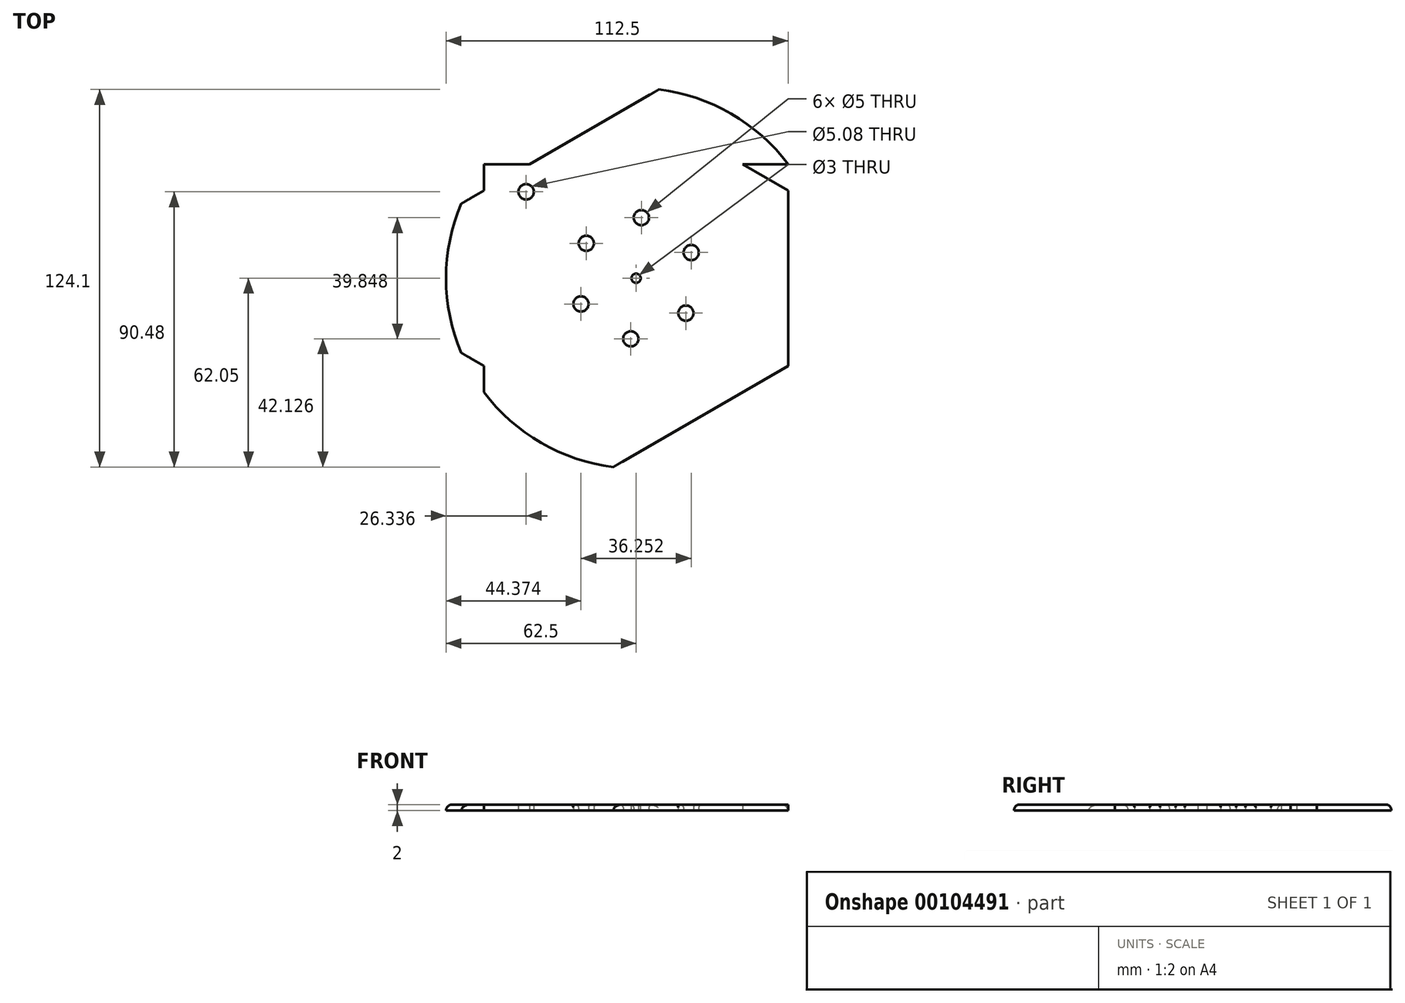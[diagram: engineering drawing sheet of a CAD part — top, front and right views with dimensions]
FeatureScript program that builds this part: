
annotation { "Feature Type Name" : "Feature", "Feature Type Description" : "" }
export const myFeature = defineFeature(function(context is Context, id is Id, definition is map)
    precondition{}
    {
        {
            var Q0;
            Q0=qCreatedBy(makeId("Top.planeOp"),FACE);
            var sketch = newSketch(context, id + "F0", { "sketchPlane" : qUnion([Q0])});
            skLineSegment(sketch, "E0.bottom", {"start": v(50, -37.5) * mm, "end": v(-50, -37.5) * mm});
            skLineSegment(sketch, "E0.top", {"start": v(50, 37.5) * mm, "end": v(-50, 37.5) * mm});
            skLineSegment(sketch, "E0.left", {"start": v(50, -37.5) * mm, "end": v(50, 37.5) * mm});
            skLineSegment(sketch, "E0.right", {"start": v(-50, -37.5) * mm, "end": v(-50, 37.5) * mm});
            skPoint(sketch, "E0.middle", {"position": v(0, 0) * mm});
            skCircle(sketch, "E1", {"center": v(-16.38, 11.47) * mm, "radius": 2.5 * mm});
            skLineSegment(sketch, "E2", {"start": v(0, 0) * mm, "end": v(-16.38, 11.47) * mm, "construction": true});
            skLineSegment(sketch, "E3", {"start": v(0, 0) * mm, "end": v(-16.38, 0) * mm, "construction": true});
            skCircle(sketch, "E4.1.0", {"center": v(-18.13, -8.45) * mm, "radius": 2.5 * mm});
            skLineSegment(sketch, "E4.1.1", {"start": v(0, 0) * mm, "end": v(-8.2, -14.19) * mm, "construction": true});
            skLineSegment(sketch, "E4.1.3", {"start": v(0, 0) * mm, "end": v(-18.13, -8.45) * mm, "construction": true});
            skLineSegment(sketch, "E4.1.4", {"start": v(7.48, -62.05) * mm, "end": v(-57.48, -24.55) * mm});
            skCircle(sketch, "E4.2.0", {"center": v(-1.74, -19.92) * mm, "radius": 2.5 * mm});
            skLineSegment(sketch, "E4.2.1", {"start": v(0, 0) * mm, "end": v(8.2, -14.19) * mm, "construction": true});
            skLineSegment(sketch, "E4.2.3", {"start": v(0, 0) * mm, "end": v(-1.74, -19.92) * mm, "construction": true});
            skLineSegment(sketch, "E4.2.4", {"start": v(57.48, -24.55) * mm, "end": v(-7.48, -62.05) * mm});
            skCircle(sketch, "E4.3.0", {"center": v(16.38, -11.47) * mm, "radius": 2.5 * mm});
            skLineSegment(sketch, "E4.3.1", {"start": v(0, 0) * mm, "end": v(16.38, 0) * mm, "construction": true});
            skLineSegment(sketch, "E4.3.3", {"start": v(0, 0) * mm, "end": v(16.38, -11.47) * mm, "construction": true});
            skLineSegment(sketch, "E4.3.4", {"start": v(50, 37.5) * mm, "end": v(50, -37.5) * mm});
            skCircle(sketch, "E4.4.0", {"center": v(18.13, 8.45) * mm, "radius": 2.5 * mm});
            skLineSegment(sketch, "E4.4.1", {"start": v(0, 0) * mm, "end": v(8.2, 14.19) * mm, "construction": true});
            skLineSegment(sketch, "E4.4.3", {"start": v(0, 0) * mm, "end": v(18.13, 8.45) * mm, "construction": true});
            skLineSegment(sketch, "E4.4.4", {"start": v(-7.48, 62.05) * mm, "end": v(57.48, 24.55) * mm});
            skCircle(sketch, "E4.5.0", {"center": v(1.74, 19.92) * mm, "radius": 2.5 * mm});
            skLineSegment(sketch, "E4.5.1", {"start": v(0, 0) * mm, "end": v(-8.2, 14.19) * mm, "construction": true});
            skLineSegment(sketch, "E4.5.3", {"start": v(0, 0) * mm, "end": v(1.74, 19.92) * mm, "construction": true});
            skLineSegment(sketch, "E4.5.4", {"start": v(-57.48, 24.55) * mm, "end": v(7.48, 62.05) * mm});
            skCircle(sketch, "E5", {"center": v(-36.16, 28.43) * mm, "radius": 2.54 * mm});
            skCircle(sketch, "E6", {"center": v(0, 0) * mm, "radius": 62.5 * mm});
            skSolve(sketch);
        }
        {
            var Q0;
            Q0=makeQuery(id+"F0.imprint","IMPRINT",FACE,{"disambiguationData":[TD([[makeQuery(id+"F0.imprint","IMPRINT",EDGE,{"derivedFrom":sQuery(id+"F0.wireOp",EDGE,"E1")}),-1.0]])]});
            var Q1;
            {var subQ0=sQuery(id+"F0.wireOp",EDGE,"E0.right");var subQ1=sQuery(id+"F0.wireOp",EDGE,"E0.bottom");var subQ2=makeQuery(id+"F0.imprint","INTERSECT",VERTEX,{"derivedFrom":[subQ1,subQ0]});Q1=makeQuery(id+"F0.imprint","IMPRINT",FACE,{"disambiguationData":[TD([[makeQuery(id+"F0.imprint","IMPRINT",EDGE,{"disambiguationData":[TD([[subQ2,1.0]])],"derivedFrom":subQ1}),-1.0]])]});}
            var Q2;
            {var subQ0=sQuery(id+"F0.wireOp",EDGE,"E0.right");var subQ1=sQuery(id+"F0.wireOp",EDGE,"E0.top");var subQ2=makeQuery(id+"F0.imprint","INTERSECT",VERTEX,{"derivedFrom":[subQ1,subQ0]});Q2=makeQuery(id+"F0.imprint","IMPRINT",FACE,{"disambiguationData":[TD([[makeQuery(id+"F0.imprint","IMPRINT",EDGE,{"disambiguationData":[TD([[subQ2,1.0]])],"derivedFrom":subQ1}),1.0]])]});}
            var Q3;
            {var subQ0=sQuery(id+"F0.wireOp",EDGE,"E4.3.4");var subQ1=sQuery(id+"F0.wireOp",EDGE,"E0.top");var subQ2=makeQuery(id+"F0.imprint","INTERSECT",VERTEX,{"derivedFrom":[subQ1,subQ0]});Q3=makeQuery(id+"F0.imprint","IMPRINT",FACE,{"disambiguationData":[TD([[makeQuery(id+"F0.imprint","IMPRINT",EDGE,{"disambiguationData":[TD([[subQ2,-1.0]])],"derivedFrom":subQ1}),1.0]])]});}
            var Q4;
            {var subQ0=sQuery(id+"F0.wireOp",EDGE,"E4.3.4");var subQ1=sQuery(id+"F0.wireOp",EDGE,"E0.bottom");var subQ2=makeQuery(id+"F0.imprint","INTERSECT",VERTEX,{"derivedFrom":[subQ1,subQ0]});Q4=makeQuery(id+"F0.imprint","IMPRINT",FACE,{"disambiguationData":[TD([[makeQuery(id+"F0.imprint","IMPRINT",EDGE,{"disambiguationData":[TD([[subQ2,-1.0]])],"derivedFrom":subQ1}),-1.0]])]});}
            var Q5;
            {var subQ0=sQuery(id+"F0.wireOp",EDGE,"E4.4.4");var subQ1=sQuery(id+"F0.wireOp",EDGE,"E0.top");var subQ2=makeQuery(id+"F0.imprint","INTERSECT",VERTEX,{"derivedFrom":[subQ1,subQ0]});Q5=makeQuery(id+"F0.imprint","IMPRINT",FACE,{"disambiguationData":[TD([[makeQuery(id+"F0.imprint","IMPRINT",EDGE,{"disambiguationData":[TD([[subQ2,-1.0]])],"derivedFrom":subQ1}),-1.0]])]});}
            var Q6;
            {var subQ0=sQuery(id+"F0.wireOp",EDGE,"E6");var subQ1=sQuery(id+"F0.wireOp",EDGE,"E4.2.4");var subQ2=makeQuery(id+"F0.imprint","INTERSECT",VERTEX,{"disambiguationData":[OD(0.0)],"derivedFrom":[subQ1,subQ0]});Q6=makeQuery(id+"F0.imprint","IMPRINT",FACE,{"disambiguationData":[TD([[makeQuery(id+"F0.imprint","IMPRINT",EDGE,{"disambiguationData":[TD([[subQ2,-1.0]])],"derivedFrom":subQ1}),-1.0]])]});}
            var Q7;
            {var subQ1=sQuery(id+"F0.wireOp",EDGE,"E0.top");var subQ3=sQuery(id+"F0.wireOp",EDGE,"E4.4.4");var subQ4=makeQuery(id+"F0.imprint","INTERSECT",VERTEX,{"derivedFrom":[subQ1,subQ3]});Q7=makeQuery(id+"F0.imprint","IMPRINT",FACE,{"disambiguationData":[TD([[makeQuery(id+"F0.imprint","IMPRINT",EDGE,{"disambiguationData":[TD([[subQ4,1.0]])],"derivedFrom":subQ3}),1.0]])]});}
            var Q8;
            {var subQ0=sQuery(id+"F0.wireOp",EDGE,"E6");var subQ1=sQuery(id+"F0.wireOp",EDGE,"E4.4.4");var subQ2=makeQuery(id+"F0.imprint","INTERSECT",VERTEX,{"disambiguationData":[OD(0.0)],"derivedFrom":[subQ1,subQ0]});Q8=makeQuery(id+"F0.imprint","IMPRINT",FACE,{"disambiguationData":[TD([[makeQuery(id+"F0.imprint","IMPRINT",EDGE,{"disambiguationData":[TD([[subQ2,-1.0]])],"derivedFrom":subQ1}),1.0]])]});}
            var Q9;
            {var subQ0=sQuery(id+"F0.wireOp",EDGE,"E6");var subQ1=sQuery(id+"F0.wireOp",EDGE,"E4.2.4");var subQ2=makeQuery(id+"F0.imprint","INTERSECT",VERTEX,{"disambiguationData":[OD(0.0)],"derivedFrom":[subQ1,subQ0]});Q9=makeQuery(id+"F0.imprint","IMPRINT",FACE,{"disambiguationData":[TD([[makeQuery(id+"F0.imprint","IMPRINT",EDGE,{"disambiguationData":[TD([[subQ2,-1.0]])],"derivedFrom":subQ1}),1.0]])]});}
            var Q10;
            {var subQ0=sQuery(id+"F0.wireOp",EDGE,"E6");var subQ5=sQuery(id+"F0.wireOp",EDGE,"E4.1.4");var subQ7=makeQuery(id+"F0.imprint","INTERSECT",VERTEX,{"disambiguationData":[OD(0.0)],"derivedFrom":[subQ5,subQ0]});Q10=makeQuery(id+"F0.imprint","IMPRINT",FACE,{"disambiguationData":[TD([[makeQuery(id+"F0.imprint","IMPRINT",EDGE,{"disambiguationData":[TD([[subQ7,-1.0]])],"derivedFrom":subQ5}),-1.0]])]});}
            var Q11;
            {var subQ0=sQuery(id+"F0.wireOp",EDGE,"E4.2.4");var subQ1=sQuery(id+"F0.wireOp",EDGE,"E0.bottom");var subQ2=makeQuery(id+"F0.imprint","INTERSECT",VERTEX,{"derivedFrom":[subQ1,subQ0]});Q11=makeQuery(id+"F0.imprint","IMPRINT",FACE,{"disambiguationData":[TD([[makeQuery(id+"F0.imprint","IMPRINT",EDGE,{"disambiguationData":[TD([[subQ2,-1.0]])],"derivedFrom":subQ1}),1.0]])]});}
            var Q12;
            {var subQ1=sQuery(id+"F0.wireOp",EDGE,"E0.bottom");var subQ3=sQuery(id+"F0.wireOp",EDGE,"E4.1.4");var subQ4=makeQuery(id+"F0.imprint","INTERSECT",VERTEX,{"derivedFrom":[subQ1,subQ3]});Q12=makeQuery(id+"F0.imprint","IMPRINT",FACE,{"disambiguationData":[TD([[makeQuery(id+"F0.imprint","IMPRINT",EDGE,{"disambiguationData":[TD([[subQ4,1.0]])],"derivedFrom":subQ3}),1.0]])]});}
            var Q13;
            {var subQ0=sQuery(id+"F0.wireOp",EDGE,"E6");var subQ3=sQuery(id+"F0.wireOp",EDGE,"E4.1.4");var subQ5=makeQuery(id+"F0.imprint","INTERSECT",VERTEX,{"disambiguationData":[OD(1.0)],"derivedFrom":[subQ3,subQ0]});Q13=makeQuery(id+"F0.imprint","IMPRINT",FACE,{"disambiguationData":[TD([[makeQuery(id+"F0.imprint","IMPRINT",EDGE,{"disambiguationData":[TD([[subQ5,1.0]])],"derivedFrom":subQ3}),1.0]])]});}
            var Q14;
            {var subQ0=sQuery(id+"F0.wireOp",EDGE,"E4.1.4");var subQ1=sQuery(id+"F0.wireOp",EDGE,"E0.right");var subQ2=makeQuery(id+"F0.imprint","INTERSECT",VERTEX,{"derivedFrom":[subQ1,subQ0]});Q14=makeQuery(id+"F0.imprint","IMPRINT",FACE,{"disambiguationData":[TD([[makeQuery(id+"F0.imprint","IMPRINT",EDGE,{"disambiguationData":[TD([[subQ2,-1.0]])],"derivedFrom":subQ1}),1.0]])]});}
            var Q15;
            {var subQ0=sQuery(id+"F0.wireOp",EDGE,"E6");var subQ1=sQuery(id+"F0.wireOp",EDGE,"E4.1.4");var subQ2=makeQuery(id+"F0.imprint","INTERSECT",VERTEX,{"disambiguationData":[OD(0.0)],"derivedFrom":[subQ1,subQ0]});Q15=makeQuery(id+"F0.imprint","IMPRINT",FACE,{"disambiguationData":[TD([[makeQuery(id+"F0.imprint","IMPRINT",EDGE,{"disambiguationData":[TD([[subQ2,-1.0]])],"derivedFrom":subQ1}),1.0]])]});}
            var Q16;
            {var subQ0=sQuery(id+"F0.wireOp",EDGE,"E6");var subQ3=sQuery(id+"F0.wireOp",EDGE,"E4.5.4");var subQ5=makeQuery(id+"F0.imprint","INTERSECT",VERTEX,{"disambiguationData":[OD(0.0)],"derivedFrom":[subQ3,subQ0]});Q16=makeQuery(id+"F0.imprint","IMPRINT",FACE,{"disambiguationData":[TD([[makeQuery(id+"F0.imprint","IMPRINT",EDGE,{"disambiguationData":[TD([[subQ5,-1.0]])],"derivedFrom":subQ3}),1.0]])]});}
            var Q17;
            {var subQ0=sQuery(id+"F0.wireOp",EDGE,"E6");var subQ5=sQuery(id+"F0.wireOp",EDGE,"E4.4.4");var subQ6=makeQuery(id+"F0.imprint","INTERSECT",VERTEX,{"disambiguationData":[OD(0.0)],"derivedFrom":[subQ5,subQ0]});Q17=makeQuery(id+"F0.imprint","IMPRINT",FACE,{"disambiguationData":[TD([[makeQuery(id+"F0.imprint","IMPRINT",EDGE,{"disambiguationData":[TD([[subQ6,-1.0]])],"derivedFrom":subQ5}),-1.0]])]});}
            var Q18;
            {var subQ0=sQuery(id+"F0.wireOp",EDGE,"E6");var subQ3=sQuery(id+"F0.wireOp",EDGE,"E4.4.4");var subQ5=makeQuery(id+"F0.imprint","INTERSECT",VERTEX,{"disambiguationData":[OD(1.0)],"derivedFrom":[subQ3,subQ0]});Q18=makeQuery(id+"F0.imprint","IMPRINT",FACE,{"disambiguationData":[TD([[makeQuery(id+"F0.imprint","IMPRINT",EDGE,{"disambiguationData":[TD([[subQ5,1.0]])],"derivedFrom":subQ3}),1.0]])]});}
            extrude(context, id + "F1", {"entities" : qUnion([Q0, Q1, Q2, Q3, Q4, Q5, Q6, Q7, Q8, Q9, Q10, Q11, Q12, Q13, Q14, Q15, Q16, Q17, Q18]), "depth" : 2 * mm});
        }
        {
            var Q0;
            Q0=makeQuery(id+"F1.opExtrude","CAP_EDGE",EDGE,{"disambiguationData":[OSD([sQuery(id+"F0.wireOp",EDGE,"E4.2.0")])],"isStart":false});
            fillet(context, id + "F2", {"entities" : qUnion([Q0]), "radius" : 1 * mm, "allowEdgeOverflow" : false});
        }
        {
            var Q0;
            Q0=makeQuery(id+"F1.opExtrude","CAP_EDGE",EDGE,{"disambiguationData":[OSD([sQuery(id+"F0.wireOp",EDGE,"E4.1.0")])],"isStart":false});
            var Q1;
            Q1=makeQuery(id+"F1.opExtrude","CAP_EDGE",EDGE,{"disambiguationData":[OSD([sQuery(id+"F0.wireOp",EDGE,"E1")])],"isStart":false});
            var Q2;
            Q2=makeQuery(id+"F1.opExtrude","CAP_EDGE",EDGE,{"disambiguationData":[OSD([sQuery(id+"F0.wireOp",EDGE,"E4.5.0")])],"isStart":false});
            var Q3;
            Q3=makeQuery(id+"F1.opExtrude","CAP_EDGE",EDGE,{"disambiguationData":[OSD([sQuery(id+"F0.wireOp",EDGE,"E4.4.0")])],"isStart":false});
            var Q4;
            Q4=makeQuery(id+"F1.opExtrude","CAP_EDGE",EDGE,{"disambiguationData":[OSD([sQuery(id+"F0.wireOp",EDGE,"E4.3.0")])],"isStart":false});
            fillet(context, id + "F3", {"entities" : qUnion([Q0, Q1, Q2, Q3, Q4]), "radius" : 1 * mm, "allowEdgeOverflow" : false});
        }
        {
            var Q0;
            Q0=makeQuery(id+"F1.opExtrude","CAP_EDGE",EDGE,{"disambiguationData":[OSD([sQuery(id+"F0.wireOp",EDGE,"E6")])],"isStart":false});
            fillet(context, id + "F4", {"entities" : qUnion([Q0]), "radius" : 2 * mm, "tangentPropagation" : true, "allowEdgeOverflow" : false});
        }
        {
            var Q0;
            Q0=makeQuery(id+"F1.opExtrude","CAP_FACE",FACE,{"disambiguationData":[OSD([sQuery(id+"F0.wireOp",EDGE,"E1"),sQuery(id+"F0.wireOp",EDGE,"E4.1.0"),sQuery(id+"F0.wireOp",EDGE,"E4.2.0"),sQuery(id+"F0.wireOp",EDGE,"E4.3.0"),sQuery(id+"F0.wireOp",EDGE,"E4.4.0"),sQuery(id+"F0.wireOp",EDGE,"E4.5.0"),sQuery(id+"F0.wireOp",EDGE,"E5"),sQuery(id+"F0.wireOp",EDGE,"E6")])],"isStart":false});
            var sketch = newSketch(context, id + "F5", { "sketchPlane" : qUnion([Q0])});
            skCircle(sketch, "E7", {"center": v(0, 0) * mm, "radius": 1.5 * mm});
            skSolve(sketch);
        }
        {
            var Q0;
            Q0=makeQuery(id+"F5.imprint","IMPRINT",FACE,{"disambiguationData":[TD([[makeQuery(id+"F5.imprint","IMPRINT",EDGE,{"derivedFrom":sQuery(id+"F5.wireOp",EDGE,"E7")}),1.0]])]});
            var Q1;
            Q1=sQuery(id+"F5.wireOp",EDGE,"E7");
            extrude(context, id + "F6", {"entities" : qUnion([Q0]), "operationType" : NewBodyOperationType.REMOVE, "surfaceEntities" : qUnion([Q1]), "oppositeDirection" : true, "depth" : 2 * mm});
        }
    });
